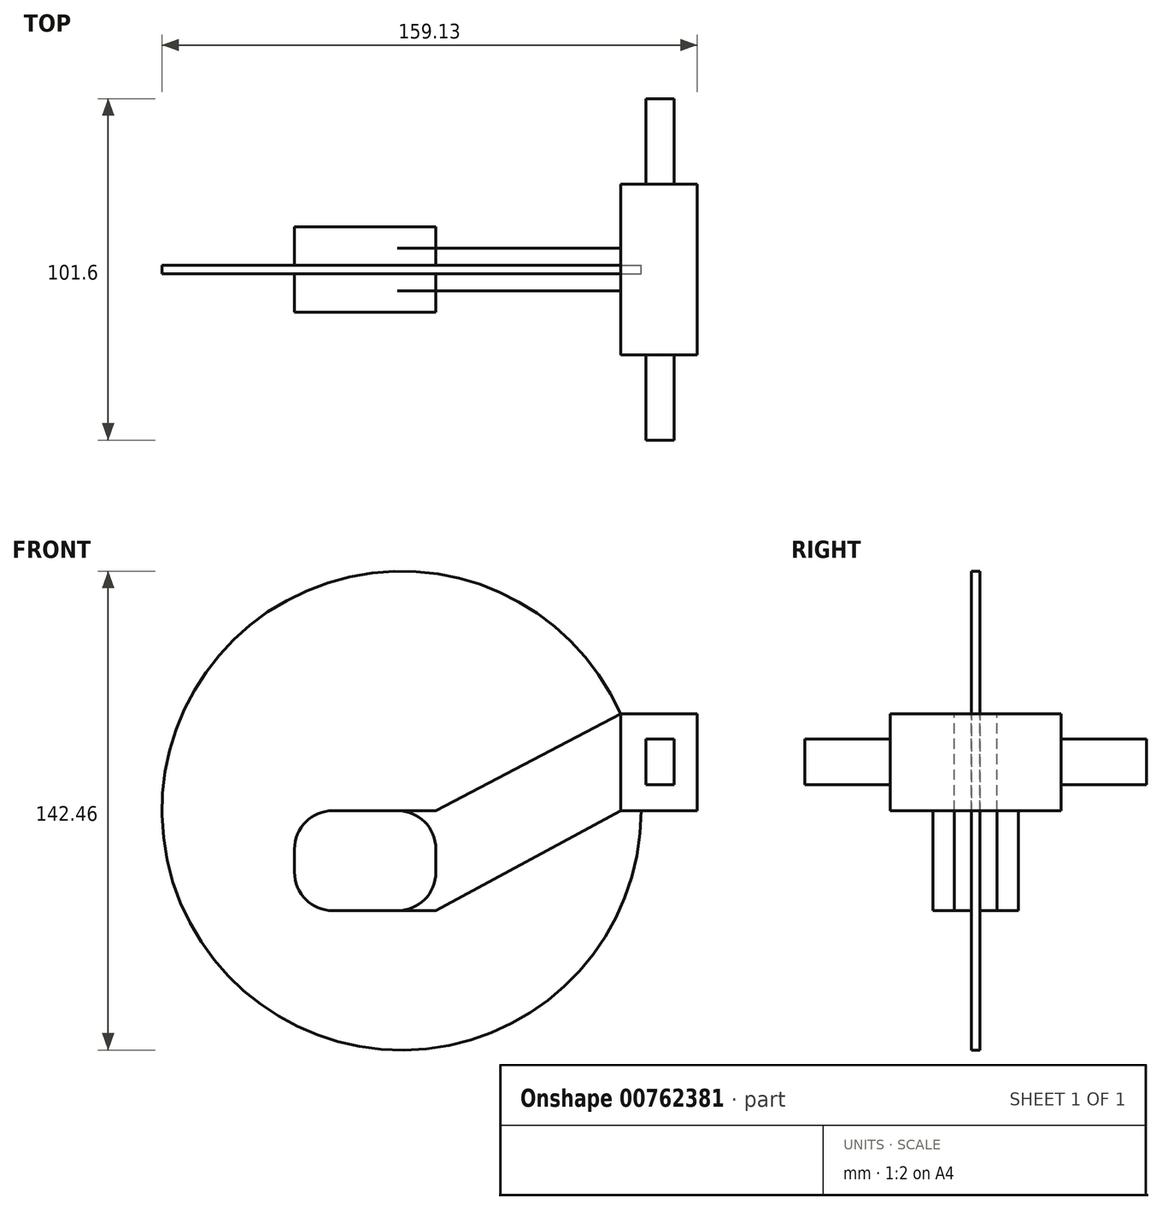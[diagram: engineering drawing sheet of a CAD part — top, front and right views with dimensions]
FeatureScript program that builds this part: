
annotation { "Feature Type Name" : "Feature", "Feature Type Description" : "" }
export const myFeature = defineFeature(function(context is Context, id is Id, definition is map)
    precondition{}
    {
        {
            var Q0;
            Q0=qCreatedBy(makeId("Front.planeOp"),FACE);
            var sketch = newSketch(context, id + "F0", { "sketchPlane" : qUnion([Q0])});
            skLineSegment(sketch, "E0.bottom", {"start": v(-23.37, 0) * mm, "end": v(-42.53, 0) * mm});
            skLineSegment(sketch, "E0.top", {"start": v(-23.37, 29.79) * mm, "end": v(-42.53, 29.79) * mm});
            skLineSegment(sketch, "E0.left", {"start": v(-11.94, 11.43) * mm, "end": v(-11.94, 18.36) * mm});
            skLineSegment(sketch, "E0.right", {"start": v(-53.96, 11.43) * mm, "end": v(-53.96, 18.36) * mm});
            skLineSegment(sketch, "E1.bottom", {"start": v(43.03, 58.55) * mm, "end": v(65.76, 58.55) * mm});
            skLineSegment(sketch, "E1.top", {"start": v(43.03, 29.79) * mm, "end": v(65.76, 29.79) * mm});
            skLineSegment(sketch, "E1.left", {"start": v(43.03, 58.55) * mm, "end": v(43.03, 29.79) * mm});
            skLineSegment(sketch, "E1.right", {"start": v(65.76, 58.55) * mm, "end": v(65.76, 29.79) * mm});
            skPoint(sketch, "E2.visualSharp", {"position": v(-11.94, 29.79) * mm});
            skArc(sketch, "E2.filletArc", {"start": v(-11.94, 18.36) * mm, "mid": v(-15.3, 26.44) * mm, "end": v(-23.37, 29.79) * mm});
            skPoint(sketch, "E3.visualSharp", {"position": v(-53.96, 0) * mm});
            skArc(sketch, "E3.filletArc", {"start": v(-53.96, 11.43) * mm, "mid": v(-50.62, 3.35) * mm, "end": v(-42.53, 0) * mm});
            skPoint(sketch, "E4.visualSharp", {"position": v(-53.96, 29.79) * mm});
            skArc(sketch, "E4.filletArc", {"start": v(-42.53, 29.79) * mm, "mid": v(-50.62, 26.44) * mm, "end": v(-53.96, 18.36) * mm});
            skPoint(sketch, "E5.visualSharp", {"position": v(-11.94, 0) * mm});
            skArc(sketch, "E5.filletArc", {"start": v(-23.37, 0) * mm, "mid": v(-15.3, 3.35) * mm, "end": v(-11.94, 11.43) * mm});
            skLineSegment(sketch, "E6", {"start": v(-11.94, 29.79) * mm, "end": v(43.03, 58.55) * mm});
            skLineSegment(sketch, "E7", {"start": v(-11.94, 0) * mm, "end": v(43.03, 29.79) * mm});
            skLineSegment(sketch, "E8", {"start": v(-11.94, 0) * mm, "end": v(-23.37, 0) * mm});
            skLineSegment(sketch, "E9", {"start": v(-11.94, 29.79) * mm, "end": v(-23.37, 29.79) * mm});
            skLineSegment(sketch, "E10.bottom", {"start": v(50.5, 51.09) * mm, "end": v(58.86, 51.09) * mm});
            skLineSegment(sketch, "E10.top", {"start": v(50.5, 37.56) * mm, "end": v(58.86, 37.56) * mm});
            skLineSegment(sketch, "E10.left", {"start": v(50.5, 51.09) * mm, "end": v(50.5, 37.56) * mm});
            skLineSegment(sketch, "E10.right", {"start": v(58.86, 51.09) * mm, "end": v(58.86, 37.56) * mm});
            skFitSpline(sketch, "E11", {"points": [v(-42.53, 29.79) * mm, v(-11.94, 29.79) * mm], "startDerivative": vector(30.59, 0) * mm, "endDerivative": vector(30.59, 0) * mm});
            skArc(sketch, "E12", {"start": v(43.03, 58.55) * mm, "mid": v(-87.65, 1.82) * mm, "end": v(43.7, 56.97) * mm});
            skSolve(sketch);
        }
        {
            var Q0;
            Q0=makeQuery(id+"F0.imprint","IMPRINT",FACE,{"disambiguationData":[TD([[makeQuery(id+"F0.imprint","IMPRINT",EDGE,{"derivedFrom":sQuery(id+"F0.wireOp",EDGE,"E0.bottom")}),-1.0]])]});
            extrude(context, id + "F1", {"entities" : qUnion([Q0]), "endBound" : BoundingType.SYMMETRIC, "depth" : 25.4 * mm, "offsetDistance" : 25.4 * mm});
        }
        {
            var Q0;
            Q0=makeQuery(id+"F0.imprint","IMPRINT",FACE,{"disambiguationData":[TD([[makeQuery(id+"F0.imprint","IMPRINT",EDGE,{"derivedFrom":sQuery(id+"F0.wireOp",EDGE,"E0.left")}),-1.0]])]});
            extrude(context, id + "F2", {"entities" : qUnion([Q0]), "operationType" : NewBodyOperationType.ADD, "endBound" : BoundingType.SYMMETRIC, "depth" : 12.7 * mm, "offsetDistance" : 25.4 * mm});
        }
        {
            var Q0;
            Q0=makeQuery(id+"F0.imprint","IMPRINT",FACE,{"disambiguationData":[TD([[makeQuery(id+"F0.imprint","IMPRINT",EDGE,{"derivedFrom":sQuery(id+"F0.wireOp",EDGE,"E1.bottom")}),-1.0]])]});
            extrude(context, id + "F3", {"entities" : qUnion([Q0]), "operationType" : NewBodyOperationType.ADD, "endBound" : BoundingType.SYMMETRIC, "depth" : 50.8 * mm, "offsetDistance" : 25.4 * mm});
        }
        {
            var Q0;
            Q0=makeQuery(id+"F0.imprint","IMPRINT",FACE,{"disambiguationData":[TD([[makeQuery(id+"F0.imprint","IMPRINT",EDGE,{"derivedFrom":sQuery(id+"F0.wireOp",EDGE,"E10.bottom")}),-1.0]])]});
            extrude(context, id + "F4", {"entities" : qUnion([Q0]), "operationType" : NewBodyOperationType.ADD, "endBound" : BoundingType.SYMMETRIC, "depth" : 101.6 * mm, "offsetDistance" : 25.4 * mm});
        }
        {
            var Q0;
            Q0=makeQuery(id+"F0.imprint","IMPRINT",FACE,{"disambiguationData":[TD([[makeQuery(id+"F0.imprint","IMPRINT",EDGE,{"derivedFrom":sQuery(id+"F0.wireOp",EDGE,"E0.bottom")}),1.0]])]});
            extrude(context, id + "F5", {"entities" : qUnion([Q0]), "operationType" : NewBodyOperationType.ADD, "endBound" : BoundingType.SYMMETRIC, "depth" : 2.54 * mm, "offsetDistance" : 25.4 * mm});
        }
    });
